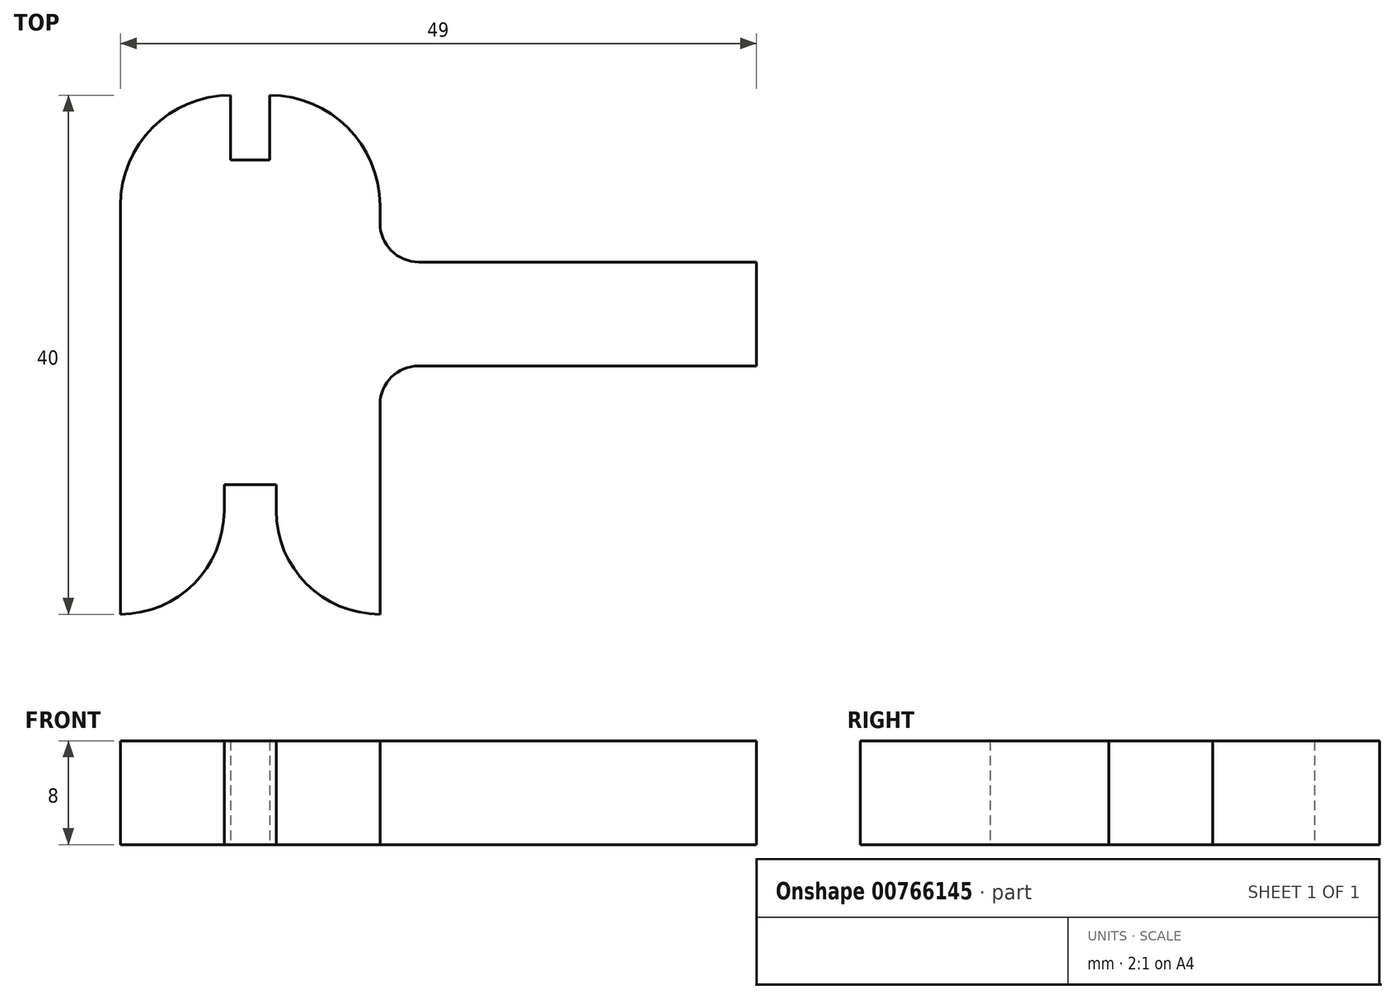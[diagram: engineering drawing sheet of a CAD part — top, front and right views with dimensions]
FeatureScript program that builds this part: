
annotation { "Feature Type Name" : "Feature", "Feature Type Description" : "" }
export const myFeature = defineFeature(function(context is Context, id is Id, definition is map)
    precondition{}
    {
        {
            var Q0;
            Q0=qCreatedBy(makeId("Top.planeOp"),FACE);
            var sketch = newSketch(context, id + "F0", { "sketchPlane" : qUnion([Q0])});
            skLineSegment(sketch, "E0", {"start": v(24.5, 7.14) * mm, "end": v(24.5, -0.86) * mm});
            skLineSegment(sketch, "E1", {"start": v(24.5, -0.86) * mm, "end": v(-1.5, -0.86) * mm});
            skArc(sketch, "E2", {"start": v(-1.5, -0.86) * mm, "mid": v(-3.62, -1.74) * mm, "end": v(-4.5, -3.86) * mm});
            skLineSegment(sketch, "E3", {"start": v(-4.5, -3.86) * mm, "end": v(-4.5, -20) * mm});
            skArc(sketch, "E4", {"start": v(-4.5, -20) * mm, "mid": v(-10.16, -17.66) * mm, "end": v(-12.5, -12) * mm});
            skLineSegment(sketch, "E5", {"start": v(-12.5, -12) * mm, "end": v(-12.5, -10) * mm});
            skLineSegment(sketch, "E6", {"start": v(-12.5, -10) * mm, "end": v(-16.5, -10) * mm});
            skLineSegment(sketch, "E7", {"start": v(-16.5, -10) * mm, "end": v(-16.5, -12) * mm});
            skArc(sketch, "E8", {"start": v(-16.5, -12) * mm, "mid": v(-18.84, -17.66) * mm, "end": v(-24.5, -20) * mm});
            skLineSegment(sketch, "E9", {"start": v(-24.5, -20) * mm, "end": v(-24.5, 11.5) * mm});
            skArc(sketch, "E10", {"start": v(-24.5, 11.5) * mm, "mid": v(-22.01, 17.51) * mm, "end": v(-16, 20) * mm});
            skLineSegment(sketch, "E11", {"start": v(-16, 20) * mm, "end": v(-16, 15) * mm});
            skLineSegment(sketch, "E12", {"start": v(-16, 15) * mm, "end": v(-13, 15) * mm});
            skLineSegment(sketch, "E13", {"start": v(-13, 15) * mm, "end": v(-13, 20) * mm});
            skArc(sketch, "E14", {"start": v(-13, 20) * mm, "mid": v(-6.99, 17.51) * mm, "end": v(-4.5, 11.5) * mm});
            skLineSegment(sketch, "E15", {"start": v(-4.5, 11.5) * mm, "end": v(-4.5, 10.14) * mm});
            skArc(sketch, "E16", {"start": v(-4.5, 10.14) * mm, "mid": v(-3.62, 8.02) * mm, "end": v(-1.5, 7.14) * mm});
            skLineSegment(sketch, "E17", {"start": v(-1.5, 7.14) * mm, "end": v(24.5, 7.14) * mm});
            skSolve(sketch);
        }
        {
            var Q0;
            Q0 = qSketchRegion(id + "F0", true);
            extrude(context, id + "F1", {"entities" : qUnion([Q0]), "depth" : 8 * mm, "offsetDistance" : 25 * mm});
        }
    });
